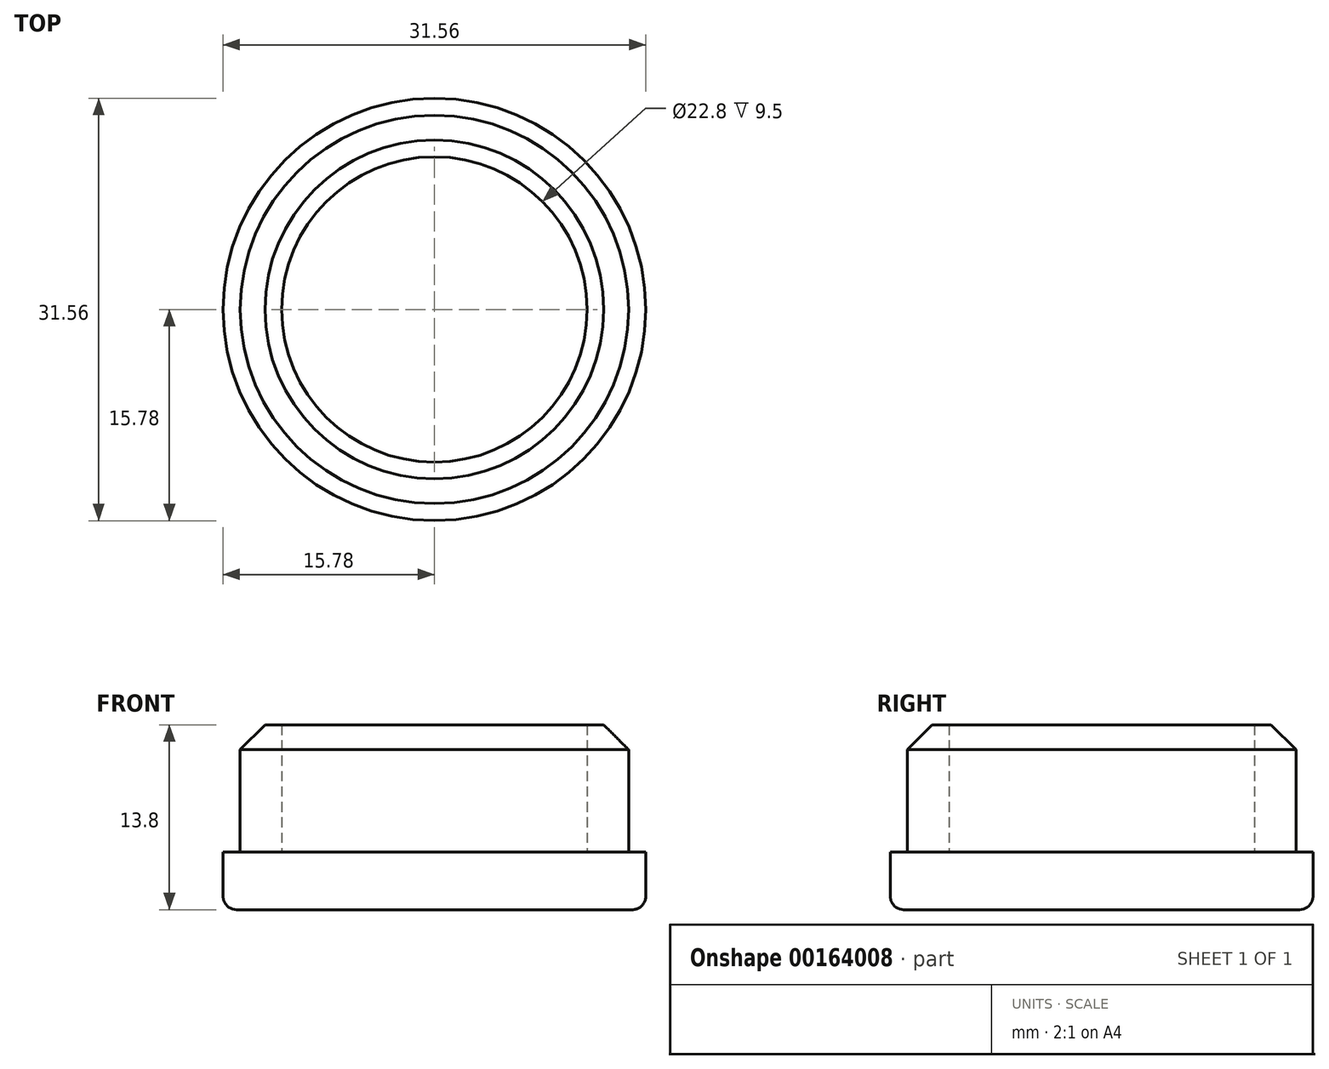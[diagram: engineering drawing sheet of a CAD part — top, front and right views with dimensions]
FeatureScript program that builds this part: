
annotation { "Feature Type Name" : "Feature", "Feature Type Description" : "" }
export const myFeature = defineFeature(function(context is Context, id is Id, definition is map)
    precondition{}
    {
        {
            var Q0;
            Q0=qCreatedBy(makeId("Top.planeOp"),FACE);
            var sketch = newSketch(context, id + "F0", { "sketchPlane" : qUnion([Q0])});
            skCircle(sketch, "E0", {"center": v(0, 0) * mm, "radius": 15.78 * mm});
            skCircle(sketch, "E1", {"center": v(0, 0) * mm, "radius": 14.5 * mm});
            skCircle(sketch, "E2", {"center": v(0, 0) * mm, "radius": 11.4 * mm});
            skSolve(sketch);
        }
        {
            var Q0;
            Q0=makeQuery(id+"F0.imprint","IMPRINT",FACE,{"disambiguationData":[TD([[makeQuery(id+"F0.imprint","IMPRINT",EDGE,{"derivedFrom":sQuery(id+"F0.wireOp",EDGE,"E2")}),1.0]])]});
            var Q1;
            Q1=makeQuery(id+"F0.imprint","IMPRINT",FACE,{"disambiguationData":[TD([[makeQuery(id+"F0.imprint","IMPRINT",EDGE,{"derivedFrom":sQuery(id+"F0.wireOp",EDGE,"E1")}),1.0]])]});
            var Q2;
            Q2=makeQuery(id+"F0.imprint","IMPRINT",FACE,{"disambiguationData":[TD([[makeQuery(id+"F0.imprint","IMPRINT",EDGE,{"derivedFrom":sQuery(id+"F0.wireOp",EDGE,"E0")}),1.0]])]});
            extrude(context, id + "F1", {"entities" : qUnion([Q0, Q1, Q2]), "depth" : 4.3 * mm});
        }
        {
            var Q0;
            Q0=makeQuery(id+"F0.imprint","IMPRINT",FACE,{"disambiguationData":[TD([[makeQuery(id+"F0.imprint","IMPRINT",EDGE,{"derivedFrom":sQuery(id+"F0.wireOp",EDGE,"E1")}),1.0]])]});
            extrude(context, id + "F2", {"entities" : qUnion([Q0]), "operationType" : NewBodyOperationType.ADD, "depth" : 13.8 * mm});
        }
        {
            var Q0;
            Q0=makeQuery(id+"F2.opExtrude","CAP_EDGE",EDGE,{"disambiguationData":[OSD([sQuery(id+"F0.wireOp",EDGE,"E1")])],"isStart":false});
            chamfer(context, id + "F3", {"entities" : qUnion([Q0]), "width" : 1.85 * mm, "tangentPropagation" : true});
        }
        {
            var Q0;
            Q0=makeQuery(id+"F1.opExtrude","CAP_EDGE",EDGE,{"disambiguationData":[OSD([sQuery(id+"F0.wireOp",EDGE,"E0")])],"isStart":true});
            fillet(context, id + "F4", {"entities" : qUnion([Q0]), "radius" : 1 * mm, "tangentPropagation" : true, "allowEdgeOverflow" : false});
        }
    });
